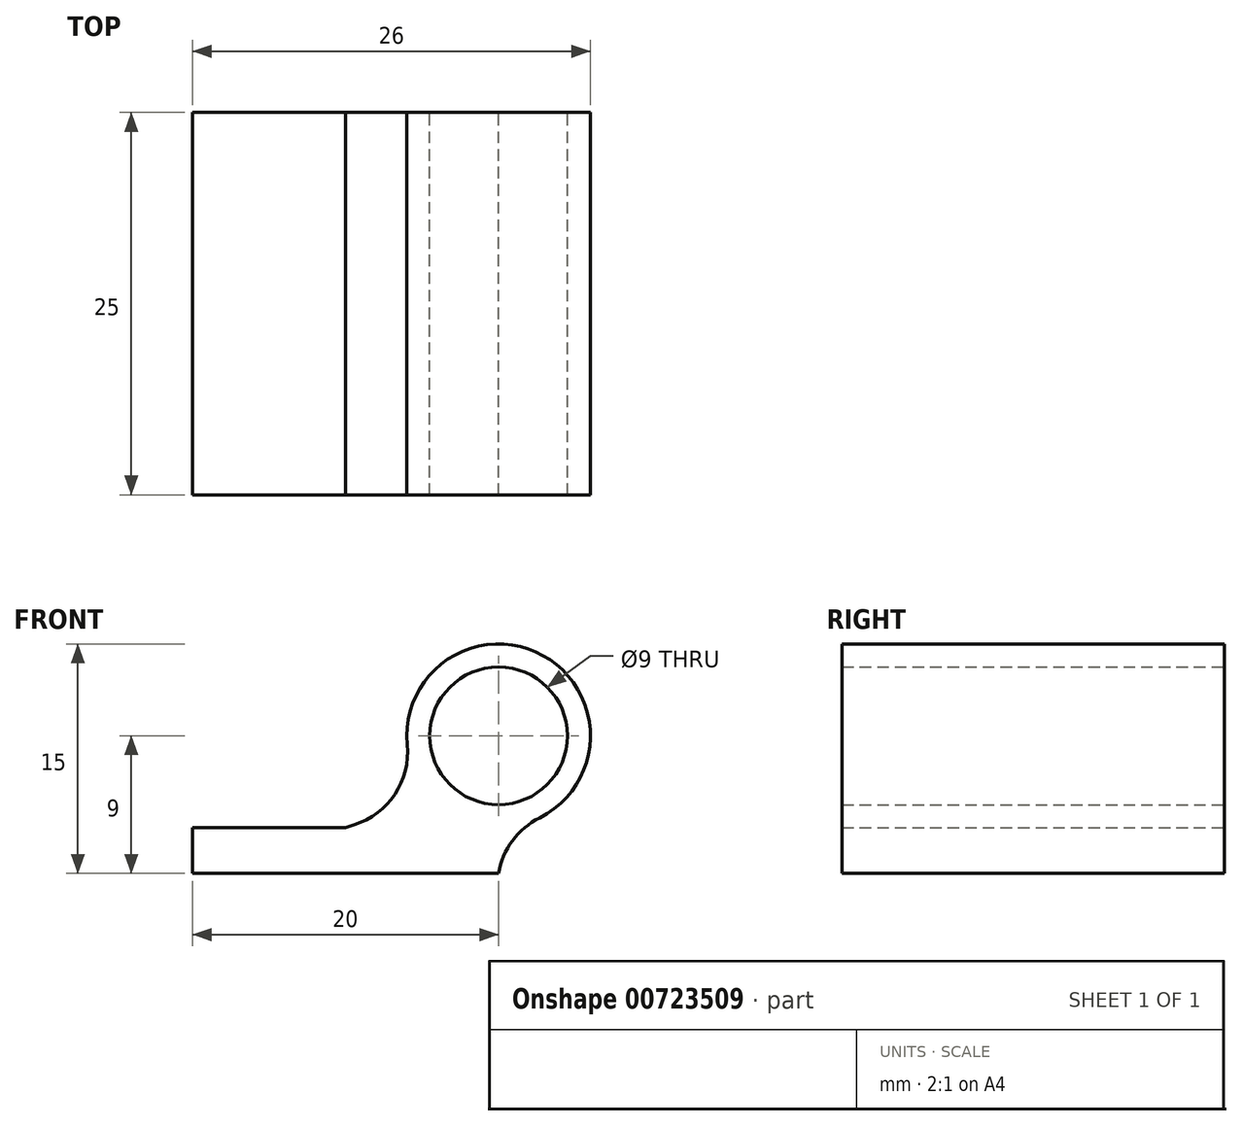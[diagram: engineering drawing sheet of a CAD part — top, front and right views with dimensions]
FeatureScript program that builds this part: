
annotation { "Feature Type Name" : "Feature", "Feature Type Description" : "" }
export const myFeature = defineFeature(function(context is Context, id is Id, definition is map)
    precondition{}
    {
        {
            var Q0;
            Q0=qCreatedBy(makeId("Front.planeOp"),FACE);
            var sketch = newSketch(context, id + "F0", { "sketchPlane" : qUnion([Q0])});
            skCircle(sketch, "E0", {"center": v(0, 0) * mm, "radius": 4.5 * mm});
            skCircle(sketch, "E1", {"center": v(0, 0) * mm, "radius": 6 * mm});
            skPoint(sketch, "E2.middle", {"position": v(0, -6) * mm});
            skLineSegment(sketch, "E3.bottom", {"start": v(0, -6) * mm, "end": v(-20, -6) * mm});
            skLineSegment(sketch, "E3.top", {"start": v(0, -9) * mm, "end": v(-20, -9) * mm});
            skLineSegment(sketch, "E3.left", {"start": v(0, -6) * mm, "end": v(0, -9) * mm});
            skLineSegment(sketch, "E3.right", {"start": v(-20, -6) * mm, "end": v(-20, -9) * mm});
            skLineSegment(sketch, "E4.MirrorCS", {"start": v(0, -6) * mm, "end": v(20, -6) * mm});
            skLineSegment(sketch, "E5.MirrorCS", {"start": v(0, -9) * mm, "end": v(20, -9) * mm});
            skLineSegment(sketch, "E6.MirrorCS", {"start": v(20, -6) * mm, "end": v(20, -9) * mm});
            skLineSegment(sketch, "E7", {"start": v(4.3, -4.19) * mm, "end": v(10, -6) * mm});
            skLineSegment(sketch, "E8.MirrorCS", {"start": v(-4.3, -4.19) * mm, "end": v(-10, -6) * mm});
            skSolve(sketch);
        }
        {
            var Q0;
            Q0=makeQuery(id+"F0.imprint","IMPRINT",FACE,{"disambiguationData":[TD([[makeQuery(id+"F0.imprint","IMPRINT",EDGE,{"derivedFrom":sQuery(id+"F0.wireOp",EDGE,"E0")}),-1.0]])]});
            var Q1;
            Q1=makeQuery(id+"F0.imprint","IMPRINT",FACE,{"disambiguationData":[TD([[makeQuery(id+"F0.imprint","IMPRINT",EDGE,{"derivedFrom":sQuery(id+"F0.wireOp",EDGE,"E3.bottom")}),1.0]])]});
            var Q2;
            {var subQ3=sQuery(id+"F0.wireOp",EDGE,"E8.MirrorCS");Q2=makeQuery(id+"F0.imprint","IMPRINT",FACE,{"disambiguationData":[TD([[makeQuery(id+"F0.imprint","IMPRINT",EDGE,{"derivedFrom":subQ3}),1.0]])]});}
            extrude(context, id + "F1", {"entities" : qUnion([Q0, Q1, Q2]), "depth" : 25 * mm, "offsetDistance" : 25 * mm});
        }
        {
            var Q0;
            Q0=makeQuery(id+"F1.opExtrude","SWEPT_EDGE",EDGE,{"disambiguationData":[OSD([sQuery(id+"F0.wireOp",EDGE,"E1"),sQuery(id+"F0.wireOp",EDGE,"E8.MirrorCS")])]});
            var Q1;
            Q1=makeQuery(id+"F1.opExtrude","SWEPT_EDGE",EDGE,{"disambiguationData":[OSD([sQuery(id+"F0.wireOp",EDGE,"E1"),sQuery(id+"F0.wireOp",EDGE,"E7")])]});
            var Q2;
            Q2=makeQuery(id+"F1.opExtrude","SWEPT_EDGE",EDGE,{"disambiguationData":[OSD([sQuery(id+"F0.wireOp",EDGE,"E1"),sQuery(id+"F0.wireOp",EDGE,"E3.bottom"),sQuery(id+"F0.wireOp",EDGE,"E3.left"),sQuery(id+"F0.wireOp",EDGE,"E4.MirrorCS")])]});
            fillet(context, id + "F2", {"entities" : qUnion([Q0, Q1, Q2]), "radius" : 5 * mm, "tangentPropagation" : true, "allowEdgeOverflow" : false});
        }
    });
